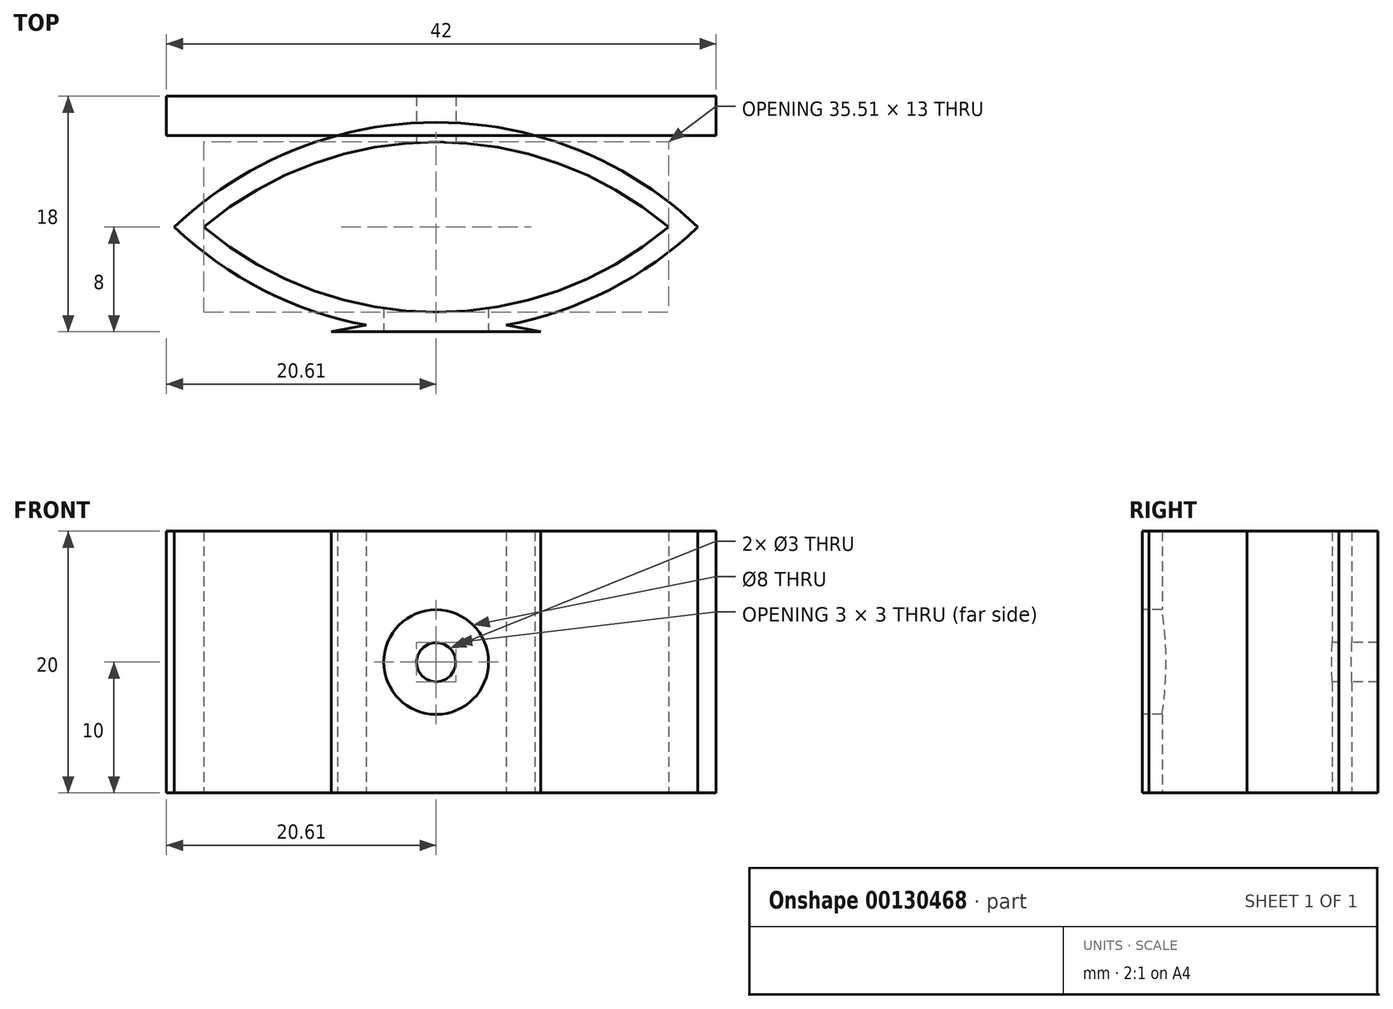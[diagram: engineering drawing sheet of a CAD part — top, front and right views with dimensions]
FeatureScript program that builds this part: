
annotation { "Feature Type Name" : "Feature", "Feature Type Description" : "" }
export const myFeature = defineFeature(function(context is Context, id is Id, definition is map)
    precondition{}
    {
        {
            var Q0;
            Q0=qCreatedBy(makeId("Top.planeOp"),FACE);
            var sketch = newSketch(context, id + "F0", { "sketchPlane" : qUnion([Q0])});
            skLineSegment(sketch, "E0", {"start": v(-20.39, -28) * mm, "end": v(19.61, -28) * mm, "construction": true});
            skLineSegment(sketch, "E1", {"start": v(-0.39, -20) * mm, "end": v(-0.39, -28) * mm, "construction": true});
            skPoint(sketch, "E2", {"position": v(-0.39, -28) * mm});
            skLineSegment(sketch, "E3", {"start": v(-0.39, -28) * mm, "end": v(-0.39, -36) * mm, "construction": true});
            skArc(sketch, "E4", {"start": v(19.61, -28) * mm, "mid": v(-0.39, -20) * mm, "end": v(-20.39, -28) * mm});
            skArc(sketch, "E5", {"start": v(-20.39, -28) * mm, "mid": v(-0.39, -36) * mm, "end": v(19.61, -28) * mm});
            skArc(sketch, "E6.0", {"start": v(17.37, -28) * mm, "mid": v(-0.39, -21.5) * mm, "end": v(-18.14, -28) * mm});
            skArc(sketch, "E6.1", {"start": v(-18.14, -28) * mm, "mid": v(-0.39, -34.5) * mm, "end": v(17.37, -28) * mm});
            skLineSegment(sketch, "E7", {"start": v(-0.39, -34.5) * mm, "end": v(-8.39, -36) * mm});
            skLineSegment(sketch, "E8", {"start": v(-8.39, -36) * mm, "end": v(7.61, -36) * mm});
            skLineSegment(sketch, "E9", {"start": v(7.61, -36) * mm, "end": v(-0.39, -34.5) * mm});
            skLineSegment(sketch, "E10", {"start": v(-21, -18) * mm, "end": v(-21, -21) * mm});
            skLineSegment(sketch, "E11", {"start": v(-21, -21) * mm, "end": v(21, -21) * mm});
            skLineSegment(sketch, "E12", {"start": v(0, 0) * mm, "end": v(0, -18) * mm});
            skLineSegment(sketch, "E13", {"start": v(0, -18) * mm, "end": v(-21, -18) * mm});
            skLineSegment(sketch, "E14", {"start": v(0, -18) * mm, "end": v(21, -18) * mm});
            skLineSegment(sketch, "E15", {"start": v(21, -18) * mm, "end": v(21, -21) * mm});
            skSolve(sketch);
        }
        {
            var Q0;
            {var subQ12=sQuery(id+"F0.wireOp",EDGE,"E6.0");Q0=makeQuery(id+"F0.imprint","IMPRINT",FACE,{"disambiguationData":[TD([[makeQuery(id+"F0.imprint","IMPRINT",EDGE,{"derivedFrom":subQ12}),-1.0]])]});}
            var Q1;
            {var subQ0=sQuery(id+"F0.wireOp",EDGE,"E8");var subQ1=sQuery(id+"F0.wireOp",EDGE,"E5");var subQ2=makeQuery(id+"F0.imprint","INTERSECT",VERTEX,{"derivedFrom":[subQ1,subQ0]});Q1=makeQuery(id+"F0.imprint","IMPRINT",FACE,{"disambiguationData":[TD([[makeQuery(id+"F0.imprint","IMPRINT",EDGE,{"disambiguationData":[TD([[subQ2,-1.0]])],"derivedFrom":subQ1}),-1.0]])]});}
            var Q2;
            {var subQ0=sQuery(id+"F0.wireOp",EDGE,"E7");var subQ1=sQuery(id+"F0.wireOp",EDGE,"E5");var subQ2=makeQuery(id+"F0.imprint","INTERSECT",VERTEX,{"derivedFrom":[subQ1,subQ0]});Q2=makeQuery(id+"F0.imprint","IMPRINT",FACE,{"disambiguationData":[TD([[makeQuery(id+"F0.imprint","IMPRINT",EDGE,{"disambiguationData":[TD([[subQ2,-1.0]])],"derivedFrom":subQ1}),-1.0]])]});}
            var Q3;
            {var subQ0=sQuery(id+"F0.wireOp",EDGE,"E7");var subQ1=sQuery(id+"F0.wireOp",EDGE,"E5");var subQ2=makeQuery(id+"F0.imprint","INTERSECT",VERTEX,{"derivedFrom":[subQ1,subQ0]});Q3=makeQuery(id+"F0.imprint","IMPRINT",FACE,{"disambiguationData":[TD([[makeQuery(id+"F0.imprint","IMPRINT",EDGE,{"disambiguationData":[TD([[subQ2,-1.0]])],"derivedFrom":subQ1}),1.0]])]});}
            var Q4;
            {var subQ0=sQuery(id+"F0.wireOp",EDGE,"E11");var subQ1=sQuery(id+"F0.wireOp",EDGE,"E4");var subQ2=makeQuery(id+"F0.imprint","INTERSECT",VERTEX,{"disambiguationData":[OD(0.0)],"derivedFrom":[subQ1,subQ0]});Q4=makeQuery(id+"F0.imprint","IMPRINT",FACE,{"disambiguationData":[TD([[makeQuery(id+"F0.imprint","IMPRINT",EDGE,{"disambiguationData":[TD([[subQ2,-1.0]])],"derivedFrom":subQ1}),1.0]])]});}
            var Q5;
            {var subQ4=sQuery(id+"F0.wireOp",EDGE,"E10");Q5=makeQuery(id+"F0.imprint","IMPRINT",FACE,{"disambiguationData":[TD([[makeQuery(id+"F0.imprint","IMPRINT",EDGE,{"derivedFrom":subQ4}),1.0]])]});}
            extrude(context, id + "F1", {"entities" : qUnion([Q0, Q1, Q2, Q3, Q4, Q5]), "depth" : 20 * mm});
        }
        {
            var Q0;
            Q0=makeQuery(id+"F1.opExtrude","SWEPT_FACE",FACE,{"disambiguationData":[OSD([sQuery(id+"F0.wireOp",EDGE,"E8")])]});
            var sketch = newSketch(context, id + "F2", { "sketchPlane" : qUnion([Q0])});
            skCircle(sketch, "E16", {"center": v(-0.39, 10) * mm, "radius": 4 * mm});
            skPoint(sketch, "E16.centerSnap0", {"position": v(-8.39, 10) * mm});
            skPoint(sketch, "E16.centerSnap1", {"position": v(-0.39, 20) * mm});
            skCircle(sketch, "E17", {"center": v(-0.39, 10) * mm, "radius": 1.5 * mm});
            skSolve(sketch);
        }
        {
            var Q0;
            Q0=qSketchRegion(id+"F2",true);
            extrude(context, id + "F3", {"entities" : qUnion([Q0]), "operationType" : NewBodyOperationType.REMOVE, "oppositeDirection" : true, "depth" : 4 * mm});
        }
        {
            var Q0;
            Q0=makeQuery(id+"F3.boolean.opBoolean","SPLIT",FACE,{"disambiguationData":[TD([makeQuery(id+"F3.opExtrude","SWEPT_FACE",FACE,{"disambiguationData":[OSD([sQuery(id+"F2.wireOp",EDGE,"E17")])]})])],"derivedFrom":makeQuery(id+"F1.opExtrude","SWEPT_FACE",FACE,{"disambiguationData":[OSD([sQuery(id+"F0.wireOp",EDGE,"E8")])]})});
            extrude(context, id + "F4", {"entities" : qUnion([Q0]), "operationType" : NewBodyOperationType.REMOVE, "oppositeDirection" : true, "depth" : 25 * mm});
        }
    });
